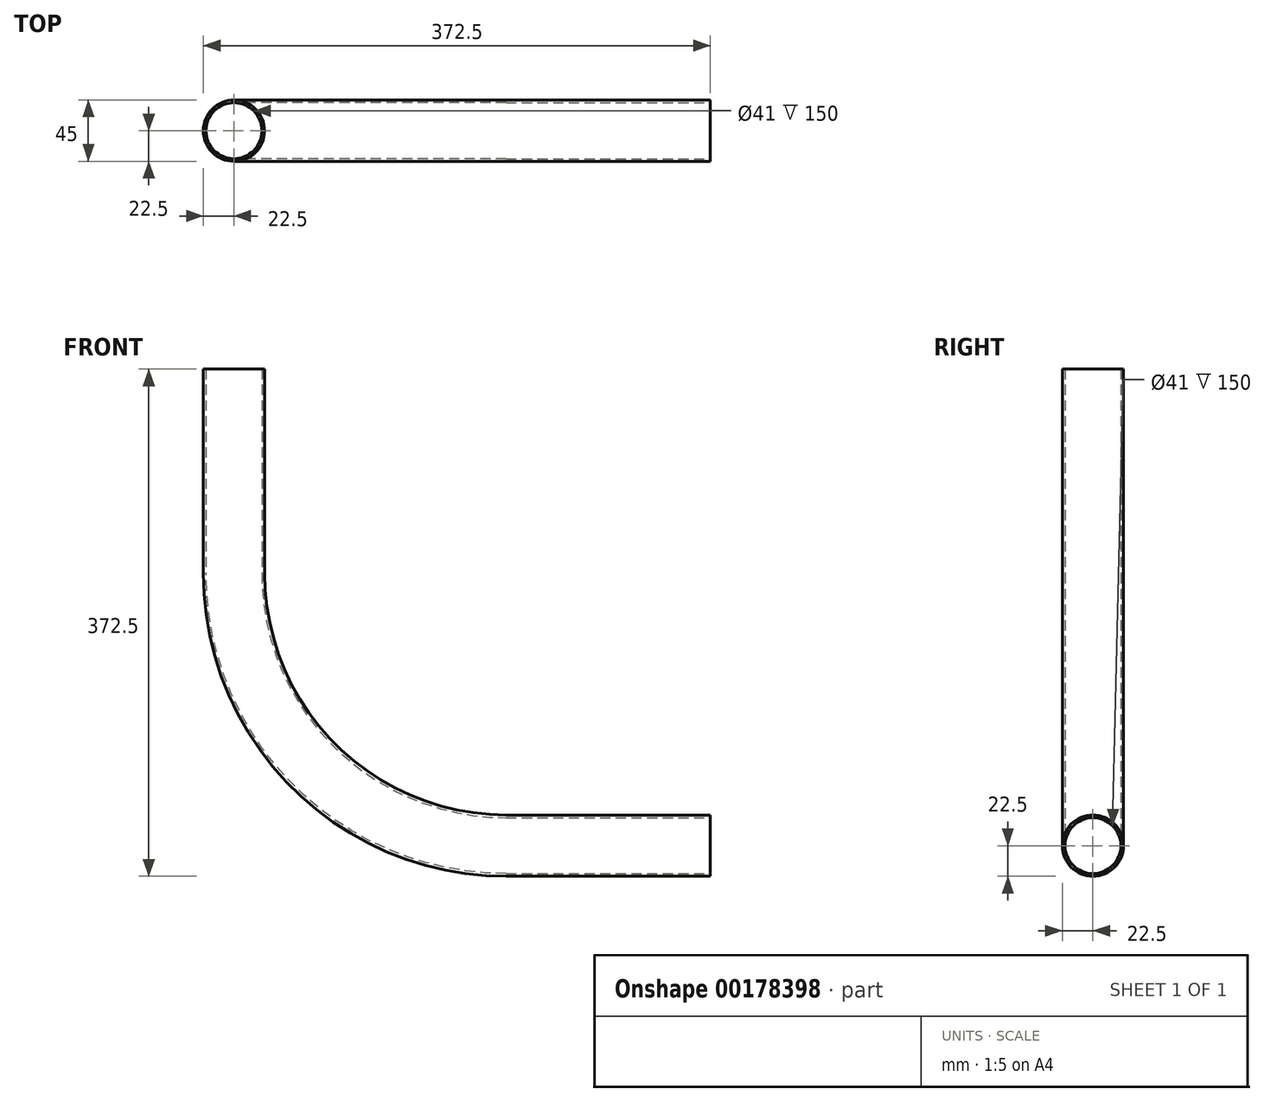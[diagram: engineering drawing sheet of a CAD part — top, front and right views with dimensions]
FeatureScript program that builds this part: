
annotation { "Feature Type Name" : "Feature", "Feature Type Description" : "" }
export const myFeature = defineFeature(function(context is Context, id is Id, definition is map)
    precondition{}
    {
        {
            var Q0;
            Q0=qCreatedBy(makeId("Front.planeOp"),FACE);
            var sketch = newSketch(context, id + "F0", { "sketchPlane" : qUnion([Q0])});
            skLineSegment(sketch, "E0", {"start": v(0, 200) * mm, "end": v(0, 350) * mm});
            skLineSegment(sketch, "E1", {"start": v(200, 0) * mm, "end": v(350, 0) * mm});
            skPoint(sketch, "E2.visualSharp", {"position": v(0, 0) * mm});
            skArc(sketch, "E2.filletArc", {"start": v(0, 200) * mm, "mid": v(58.58, 58.58) * mm, "end": v(200, 0) * mm});
            skSolve(sketch);
        }
        {
            var Q0;
            Q0=sQuery(id+"F0.wireOp",VERTEX,"E0.end");
            var Q1;
            Q1=qCreatedBy(makeId("Top.planeOp"),FACE);
            cPlane(context, id + "F1", {"entities" : qUnion([Q0, Q1]), "cplaneType" : CPlaneType.PLANE_POINT, "offset" : 25 * mm, "width" : 150 * mm, "height" : 150 * mm});
        }
        {
            var Q0;
            Q0=qCreatedBy(id+"F1.planeOp",FACE);
            var sketch = newSketch(context, id + "F2", { "sketchPlane" : qUnion([Q0])});
            skCircle(sketch, "E3", {"center": v(0, 0) * mm, "radius": 22.5 * mm});
            skCircle(sketch, "E4.0", {"center": v(0, 0) * mm, "radius": 20.5 * mm});
            skSolve(sketch);
        }
        {
            var Q0;
            Q0=makeQuery(id+"F2.imprint","IMPRINT",FACE,{"disambiguationData":[TD([[makeQuery(id+"F2.imprint","IMPRINT",EDGE,{"derivedFrom":sQuery(id+"F2.wireOp",EDGE,"E3")}),1.0]])]});
            var Q1;
            Q1=sQuery(id+"F0.wireOp",EDGE,"E0");
            var Q2;
            Q2=sQuery(id+"F0.wireOp",EDGE,"E2.filletArc");
            var Q3;
            Q3=sQuery(id+"F0.wireOp",EDGE,"E1");
            sweep(context, id + "F3", {"profiles" : qUnion([Q0]), "path" : qUnion([Q1, Q2, Q3])});
        }
    });
